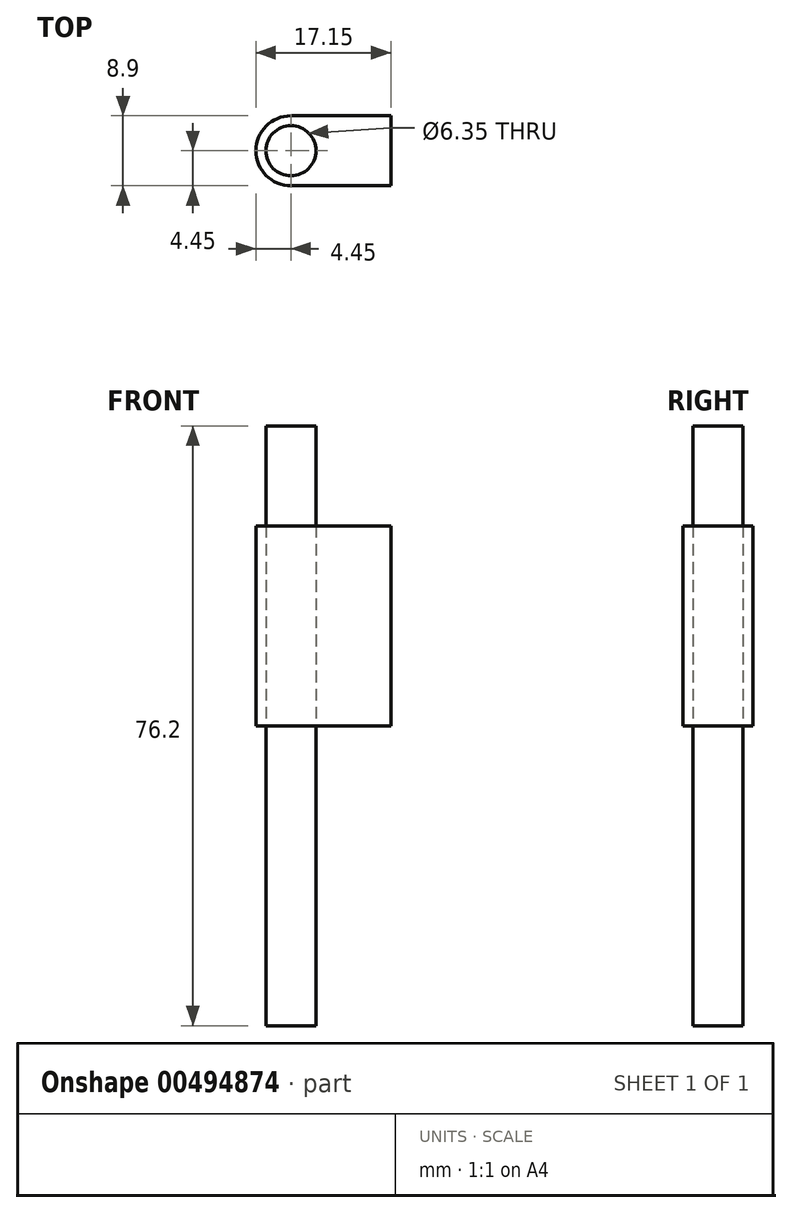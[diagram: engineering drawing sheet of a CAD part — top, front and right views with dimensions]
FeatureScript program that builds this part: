
annotation { "Feature Type Name" : "Feature", "Feature Type Description" : "" }
export const myFeature = defineFeature(function(context is Context, id is Id, definition is map)
    precondition{}
    {
        {
            var Q0;
            Q0=qCreatedBy(makeId("Top.planeOp"),FACE);
            var sketch = newSketch(context, id + "F0", { "sketchPlane" : qUnion([Q0])});
            skCircle(sketch, "E0", {"center": v(0, 0) * mm, "radius": 3.18 * mm});
            skArc(sketch, "E1", {"start": v(0, 4.45) * mm, "mid": v(-4.45, 0) * mm, "end": v(0, -4.45) * mm});
            skLineSegment(sketch, "E2", {"start": v(0, 4.45) * mm, "end": v(12.7, 4.45) * mm});
            skLineSegment(sketch, "E3", {"start": v(12.7, 4.45) * mm, "end": v(12.7, -4.44) * mm});
            skLineSegment(sketch, "E4", {"start": v(12.7, -4.44) * mm, "end": v(0, -4.45) * mm});
            skSolve(sketch);
        }
        {
            var Q0;
            Q0 = qSketchRegion(id + "F0", true);
            extrude(context, id + "F1", {"entities" : qUnion([Q0]), "depth" : 25.4 * mm});
        }
        {
            var Q0;
            Q0=makeQuery(id+"F0.imprint","IMPRINT",FACE,{"disambiguationData":[TD([[makeQuery(id+"F0.imprint","IMPRINT",EDGE,{"derivedFrom":sQuery(id+"F0.wireOp",EDGE,"E0")}),1.0]])]});
            extrude(context, id + "F2", {"entities" : qUnion([Q0]), "endBound" : BoundingType.SYMMETRIC, "depth" : 76.2 * mm});
        }
    });
